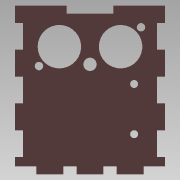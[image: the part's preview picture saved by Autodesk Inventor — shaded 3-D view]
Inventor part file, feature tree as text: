
AUTODESK INVENTOR PART (.ipt)
format: ipt  version: 2015 SP1 (Build 190203100, 203)  size: 154,112 bytes
history: native  units: mm
features: extrude x1, sketch x1
ambient origin geometry x8: Origin, YZ Plane, XZ Plane, XY Plane, X Axis, Y Axis, Z Axis, Center Point
bodies: Body1 (feature_tree)
feature tree (2):
  extrude  "Extrusion3"  Depth=20.0mm
  sketch  "Sketch1"  dims[d2=3.0mm d3=20.0mm d5=15.0mm d6=20.0mm d8=15.0mm d11=10.0mm d12=5.0mm d13=10.0mm d16=3.0mm d17=3.0mm d20=3.0mm d21=0.0mm]
